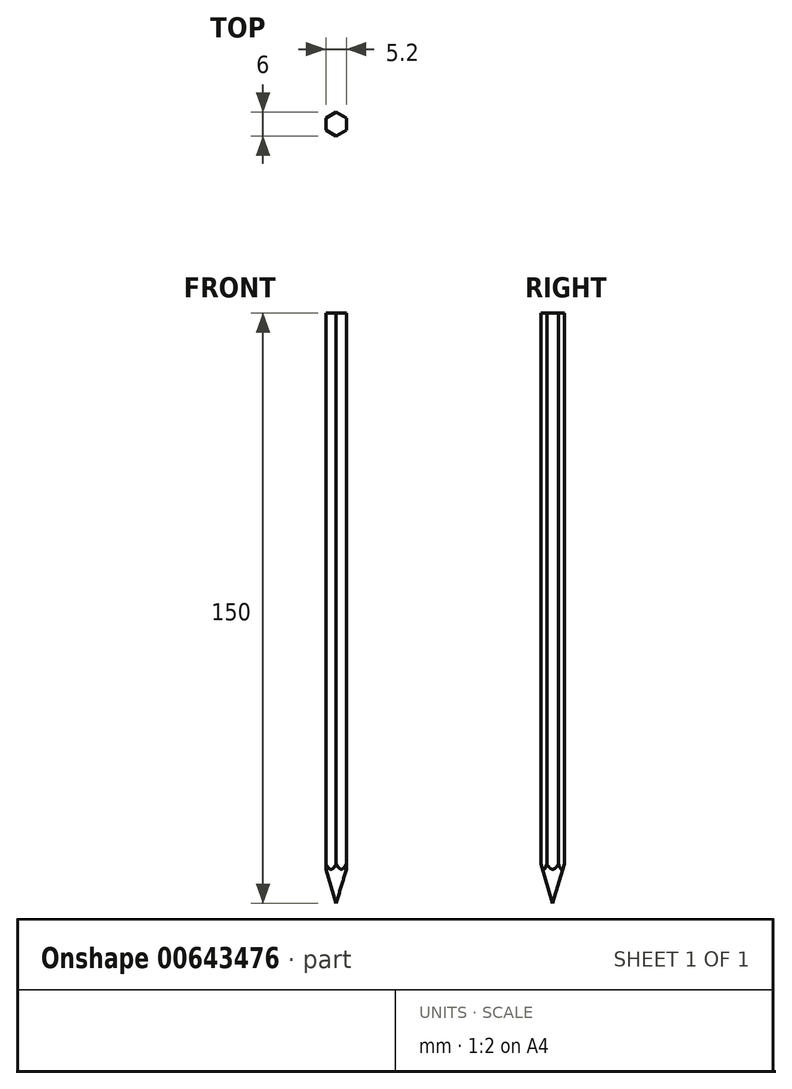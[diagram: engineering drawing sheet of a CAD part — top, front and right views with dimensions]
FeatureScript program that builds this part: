
annotation { "Feature Type Name" : "Feature", "Feature Type Description" : "" }
export const myFeature = defineFeature(function(context is Context, id is Id, definition is map)
    precondition{}
    {
        {
            var Q0;
            Q0=qCreatedBy(makeId("Top.planeOp"),FACE);
            var sketch = newSketch(context, id + "F0", { "sketchPlane" : qUnion([Q0])});
            skCircle(sketch, "E0.cCircle", {"center": v(0, 0) * mm, "radius": 3 * mm, "construction": true});
            skLineSegment(sketch, "E0.0", {"start": v(0, 3) * mm, "end": v(2.6, 1.5) * mm});
            skLineSegment(sketch, "E0.1", {"start": v(2.6, 1.5) * mm, "end": v(2.6, -1.5) * mm});
            skLineSegment(sketch, "E0.2", {"start": v(2.6, -1.5) * mm, "end": v(0, -3) * mm});
            skLineSegment(sketch, "E0.3", {"start": v(0, -3) * mm, "end": v(-2.6, -1.5) * mm});
            skLineSegment(sketch, "E0.4", {"start": v(-2.6, -1.5) * mm, "end": v(-2.6, 1.5) * mm});
            skLineSegment(sketch, "E0.5", {"start": v(-2.6, 1.5) * mm, "end": v(0, 3) * mm});
            skSolve(sketch);
        }
        {
            var Q0;
            Q0 = qSketchRegion(id + "F0", true);
            extrude(context, id + "F1", {"entities" : qUnion([Q0]), "depth" : 150 * mm, "offsetDistance" : 25 * mm});
        }
        {
            var Q0;
            Q0=makeQuery(id+"F1.opExtrude","CAP_FACE",FACE,{"disambiguationData":[OSD([sQuery(id+"F0.wireOp",EDGE,"E0.0"),sQuery(id+"F0.wireOp",EDGE,"E0.1"),sQuery(id+"F0.wireOp",EDGE,"E0.2"),sQuery(id+"F0.wireOp",EDGE,"E0.3"),sQuery(id+"F0.wireOp",EDGE,"E0.4"),sQuery(id+"F0.wireOp",EDGE,"E0.5")])],"isStart":false});
            var sketch = newSketch(context, id + "F2", { "sketchPlane" : qUnion([Q0])});
            skPoint(sketch, "E1", {"position": v(0, 0) * mm});
            skCircle(sketch, "E2", {"center": v(0, 0) * mm, "radius": 2.6 * mm});
            skSolve(sketch);
        }
        {
            var Q0;
            Q0=makeQuery(id+"F1.opExtrude","SWEPT_FACE",FACE,{"disambiguationData":[OSD([sQuery(id+"F0.wireOp",EDGE,"E0.2")])]});
            var sketch = newSketch(context, id + "F3", { "sketchPlane" : qUnion([Q0])});
            skLineSegment(sketch, "E3", {"start": v(0, 150) * mm, "end": v(0, 140) * mm});
            skLineSegment(sketch, "E4", {"start": v(0, 140) * mm, "end": v(-1.5, 140) * mm});
            skLineSegment(sketch, "E5", {"start": v(-1.5, 140) * mm, "end": v(1.5, 140) * mm});
            skSolve(sketch);
        }
        {
            var Q0;
            Q0=sQuery(id+"F3.wireOp",VERTEX,"E4.start");
            var Q1;
            Q1=sQuery(id+"F3.wireOp",VERTEX,"E3.start");
            var Q2;
            Q2=sQuery(id+"F2.wireOp",VERTEX,"E1");
            cPlane(context, id + "F4", {"entities" : qUnion([Q0, Q1, Q2]), "cplaneType" : CPlaneType.THREE_POINT, "offset" : 25 * mm, "width" : 150 * mm, "height" : 150 * mm});
        }
        {
            var Q0;
            Q0=qCreatedBy(id+"F4.planeOp",FACE);
            var sketch = newSketch(context, id + "F5", { "sketchPlane" : qUnion([Q0])});
            skLineSegment(sketch, "E6", {"start": v(0, 0) * mm, "end": v(0, 10) * mm});
            skLineSegment(sketch, "E7", {"start": v(0, 10) * mm, "end": v(-3, 10) * mm});
            skLineSegment(sketch, "E8", {"start": v(0, 0) * mm, "end": v(-3, 10) * mm});
            skLineSegment(sketch, "E9", {"start": v(0, 0) * mm, "end": v(-57.47, 191.57) * mm});
            skLineSegment(sketch, "E10", {"start": v(-57.47, 191.57) * mm, "end": v(0, 191.57) * mm});
            skSolve(sketch);
        }
        {
            var Q0;
            Q0=sQuery(id+"F5.wireOp",EDGE,"E10");
            cPlane(context, id + "F6", {"entities" : qUnion([Q0]), "cplaneType" : CPlaneType.LINE_ANGLE, "offset" : 25 * mm, "angle" : 0 * degree, "width" : 150 * mm, "height" : 150 * mm});
        }
        {
            var Q0;
            Q0=qCreatedBy(id+"F6.planeOp",FACE);
            var sketch = newSketch(context, id + "F7", { "sketchPlane" : qUnion([Q0])});
            skCircle(sketch, "E11", {"center": v(0, 0) * mm, "radius": 57.47 * mm});
            skSolve(sketch);
        }
        {
            var Q1;
            Q1=makeQuery(id+"F7.imprint","IMPRINT",FACE,{"disambiguationData":[TD([[makeQuery(id+"F7.imprint","IMPRINT",EDGE,{"derivedFrom":sQuery(id+"F7.wireOp",EDGE,"E11")}),1.0]])]});
            var Q2;
            Q2=sQuery(id+"F5.wireOp",VERTEX,"E6.start");
            loft(context, id + "F8", {"operationType" : NewBodyOperationType.INTERSECT, "sheetProfilesArray" : [{ "sheetProfileEntities" : qUnion([Q1]) }, { "sheetProfileEntities" : qUnion([Q2]) }]});
        }
    });
